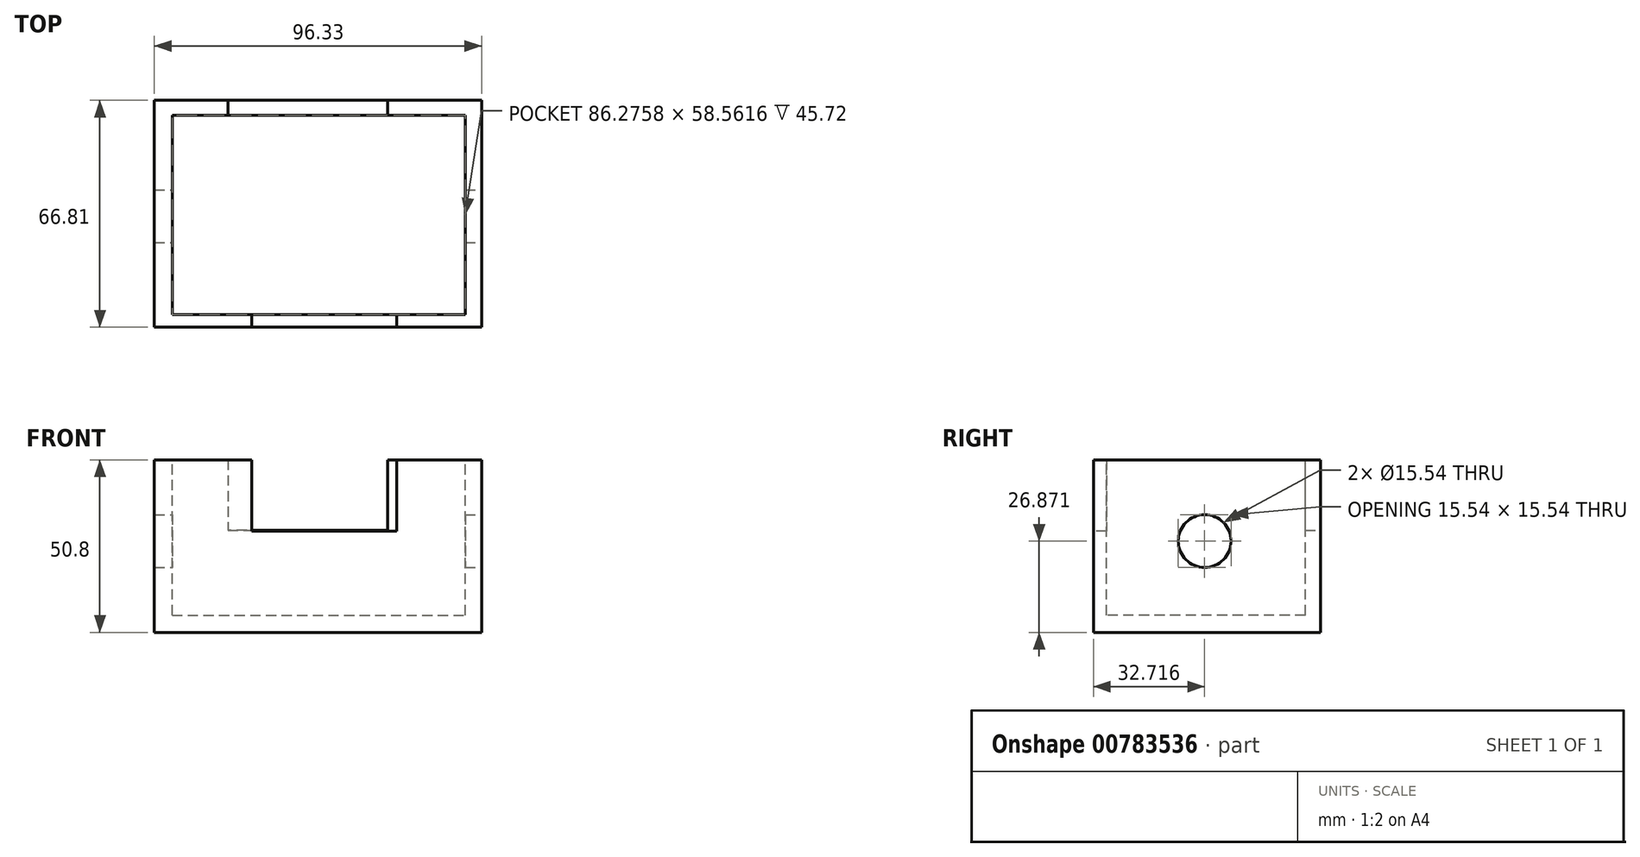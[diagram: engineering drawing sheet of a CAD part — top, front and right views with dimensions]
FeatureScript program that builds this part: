
annotation { "Feature Type Name" : "Feature", "Feature Type Description" : "" }
export const myFeature = defineFeature(function(context is Context, id is Id, definition is map)
    precondition{}
    {
        {
            var Q0;
            Q0=qCreatedBy(makeId("Top.planeOp"),FACE);
            var sketch = newSketch(context, id + "F0", { "sketchPlane" : qUnion([Q0])});
            skLineSegment(sketch, "E0.bottom", {"start": v(-49.21, 45.3) * mm, "end": v(47.12, 45.3) * mm});
            skLineSegment(sketch, "E0.top", {"start": v(-49.21, -21.5) * mm, "end": v(47.12, -21.5) * mm});
            skLineSegment(sketch, "E0.left", {"start": v(-49.21, 45.3) * mm, "end": v(-49.21, -21.5) * mm});
            skLineSegment(sketch, "E0.right", {"start": v(47.12, 45.3) * mm, "end": v(47.12, -21.5) * mm});
            skSolve(sketch);
        }
        {
            var Q0;
            Q0=makeQuery(id+"F0.imprint","IMPRINT",FACE,{"disambiguationData":[TD([[makeQuery(id+"F0.imprint","IMPRINT",EDGE,{"derivedFrom":sQuery(id+"F0.wireOp",EDGE,"E0.bottom")}),-1.0]])]});
            extrude(context, id + "F1", {"entities" : qUnion([Q0]), "depth" : 50.8 * mm, "offsetDistance" : 25.4 * mm});
        }
        {
            var Q0;
            Q0=makeQuery(id+"F1.opExtrude","CAP_FACE",FACE,{"disambiguationData":[OSD([sQuery(id+"F0.wireOp",EDGE,"E0.bottom"),sQuery(id+"F0.wireOp",EDGE,"E0.top"),sQuery(id+"F0.wireOp",EDGE,"E0.left"),sQuery(id+"F0.wireOp",EDGE,"E0.right")])],"isStart":false});
            var sketch = newSketch(context, id + "F2", { "sketchPlane" : qUnion([Q0])});
            skLineSegment(sketch, "E1.bottom", {"start": v(-43.98, 40.85) * mm, "end": v(42.3, 40.85) * mm});
            skLineSegment(sketch, "E1.top", {"start": v(-43.98, -17.71) * mm, "end": v(42.3, -17.71) * mm});
            skLineSegment(sketch, "E1.left", {"start": v(-43.98, 40.85) * mm, "end": v(-43.98, -17.71) * mm});
            skLineSegment(sketch, "E1.right", {"start": v(42.3, 40.85) * mm, "end": v(42.3, -17.71) * mm});
            skSolve(sketch);
        }
        {
            var Q0;
            Q0=makeQuery(id+"F2.imprint","IMPRINT",FACE,{"disambiguationData":[TD([[makeQuery(id+"F2.imprint","IMPRINT",EDGE,{"derivedFrom":sQuery(id+"F2.wireOp",EDGE,"E1.bottom")}),-1.0]])]});
            extrude(context, id + "F3", {"entities" : qUnion([Q0]), "operationType" : NewBodyOperationType.REMOVE, "oppositeDirection" : true, "depth" : 45.72 * mm, "offsetDistance" : 25.4 * mm});
        }
        {
            var Q0;
            Q0=makeQuery(id+"F1.opExtrude","SWEPT_FACE",FACE,{"disambiguationData":[OSD([sQuery(id+"F0.wireOp",EDGE,"E0.top")])]});
            var sketch = newSketch(context, id + "F4", { "sketchPlane" : qUnion([Q0])});
            skLineSegment(sketch, "E2.bottom", {"start": v(-20.6, 50.8) * mm, "end": v(22.05, 50.8) * mm});
            skLineSegment(sketch, "E2.top", {"start": v(-20.6, 29.81) * mm, "end": v(22.05, 29.81) * mm});
            skLineSegment(sketch, "E2.left", {"start": v(-20.6, 50.8) * mm, "end": v(-20.6, 29.81) * mm});
            skLineSegment(sketch, "E2.right", {"start": v(22.05, 50.8) * mm, "end": v(22.05, 29.81) * mm});
            skSolve(sketch);
        }
        {
            var Q0;
            Q0=makeQuery(id+"F4.imprint","IMPRINT",FACE,{"disambiguationData":[TD([[makeQuery(id+"F4.imprint","IMPRINT",EDGE,{"derivedFrom":sQuery(id+"F4.wireOp",EDGE,"E2.bottom")}),-1.0]])]});
            extrude(context, id + "F5", {"entities" : qUnion([Q0]), "operationType" : NewBodyOperationType.REMOVE, "oppositeDirection" : true, "depth" : 25.4 * mm, "offsetDistance" : 25.4 * mm});
        }
        {
            var Q0;
            Q0=makeQuery(id+"F1.opExtrude","SWEPT_FACE",FACE,{"disambiguationData":[OSD([sQuery(id+"F0.wireOp",EDGE,"E0.bottom")])]});
            var sketch = newSketch(context, id + "F6", { "sketchPlane" : qUnion([Q0])});
            skLineSegment(sketch, "E3.bottom", {"start": v(-19.4, 50.8) * mm, "end": v(27.6, 50.8) * mm});
            skLineSegment(sketch, "E3.top", {"start": v(-19.4, 30) * mm, "end": v(27.6, 30) * mm});
            skLineSegment(sketch, "E3.left", {"start": v(-19.4, 50.8) * mm, "end": v(-19.4, 30) * mm});
            skLineSegment(sketch, "E3.right", {"start": v(27.6, 50.8) * mm, "end": v(27.6, 30) * mm});
            skSolve(sketch);
        }
        {
            var Q0;
            Q0=makeQuery(id+"F6.imprint","IMPRINT",FACE,{"disambiguationData":[TD([[makeQuery(id+"F6.imprint","IMPRINT",EDGE,{"derivedFrom":sQuery(id+"F6.wireOp",EDGE,"E3.bottom")}),1.0]])]});
            extrude(context, id + "F7", {"entities" : qUnion([Q0]), "operationType" : NewBodyOperationType.REMOVE, "oppositeDirection" : true, "depth" : 25.4 * mm, "offsetDistance" : 25.4 * mm});
        }
        {
            var Q0;
            Q0=makeQuery(id+"F1.opExtrude","SWEPT_FACE",FACE,{"disambiguationData":[OSD([sQuery(id+"F0.wireOp",EDGE,"E0.right")])]});
            var sketch = newSketch(context, id + "F8", { "sketchPlane" : qUnion([Q0])});
            skCircle(sketch, "E4", {"center": v(11.2, 26.87) * mm, "radius": 7.77 * mm});
            skSolve(sketch);
        }
        {
            var Q0;
            Q0=makeQuery(id+"F8.imprint","IMPRINT",FACE,{"disambiguationData":[TD([[makeQuery(id+"F8.imprint","IMPRINT",EDGE,{"derivedFrom":sQuery(id+"F8.wireOp",EDGE,"E4")}),1.0]])]});
            extrude(context, id + "F9", {"entities" : qUnion([Q0]), "operationType" : NewBodyOperationType.REMOVE, "oppositeDirection" : true, "depth" : 127 * mm, "offsetDistance" : 25.4 * mm});
        }
    });
